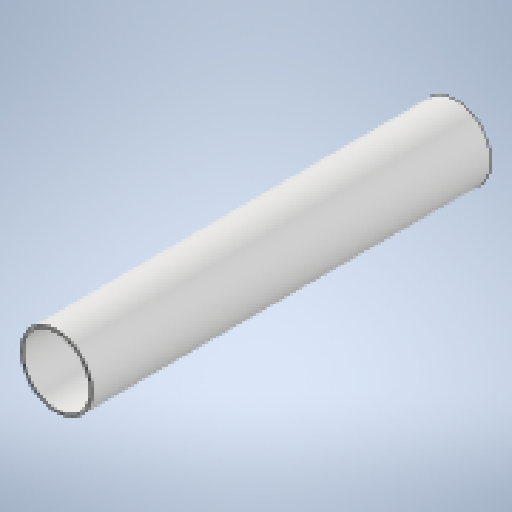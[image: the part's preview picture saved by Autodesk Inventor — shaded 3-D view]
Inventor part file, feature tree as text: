
AUTODESK INVENTOR PART (.ipt)
format: ipt  version: 2025.1 (Build 291241020, 241B)  size: 141,824 bytes
history: native  units: mm
features: extrude x1, sketch x1
ambient origin geometry x8: Origin, YZ Plane, XZ Plane, XY Plane, X Axis, Y Axis, Z Axis, Center Point
bodies: Solid1 (feature_tree)
feature tree (2):
  extrude  "Extrusion1"  Depth=442.0mm
  sketch  "Sketch1"  dims[d0=90.0mm d1=3.0mm d2=442.0mm d3=0.0mm]
